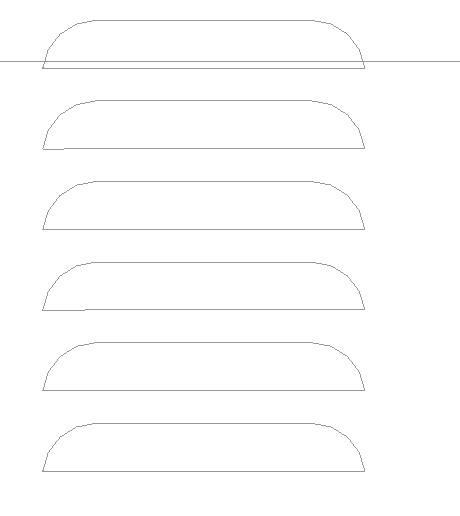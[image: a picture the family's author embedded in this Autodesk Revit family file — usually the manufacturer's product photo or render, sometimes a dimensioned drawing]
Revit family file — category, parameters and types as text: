
# Revit family: BoxAir_60-90_Inverter-P_ENG-RFA-2022
name_source: partatom
category: Mechanické zařízení
units: mm (PartAtom-declared; Revit-internal decimal feet)

## family parameters
Bod výpočtu místnosti = Ne
Kóta kulaté spojky = Použít průměr
Nadpis OmniClass = Climate Control (HVAC)
Ořezat dutým tvarem při načtení = Ne
Sdílené = Ne
Typ dílu = Normální
Vždy vertikální = Ano
Zachovat orientaci poznámky = Ne
Založené na pracovní rovině = Ne
Číslo OmniClass = 23.75.00.00

## types (2) — shared parameters
Hot water – inlet = 1'' (OD)
Hot water – outlet = 1'' (OD)
MT_CI diameter = 28 mm  [stored 0.0918635 ft]
MT_CO diameter = 28 mm  [stored 0.0918635 ft]
MT_active power = 0 W
MT_angle offset = 60 mm  [stored 0.19685 ft]
MT_apparent power = 0 VA
MT_case mat = MT_RAL7016
MT_clearance back = 250 mm  [stored 0.82021 ft]
MT_clearance top = 1500 mm  [stored 4.92126 ft]
MT_frequency (Hz) = 50 Hz
MT_ground height = 173 mm  [stored 0.567585 ft]
MT_pipe mat = MT_angle-corner
MT_voltage (V) = 400 V
Popis = Air-to-water heat pump (R290)
URL = https://www.mastertherm.eu
Výrobce = Master Therm
zero-valued in all types: Cena, MT_CosPhi, Výchozí výška

## per-type parameters (varying)
- BA60IP: El. connection=1xPG21; 1xPG29; Komentáře k typům=COMPRESSOR: BLDC Inverter; 15 – 120 rps; oil (HAF68D1U) – 2.0 l; max. op. current – 24 A; EVAPORATOR: Coil (Al/Cu); heat transfer area – 84 m2; fin spacing – 2.0 mm; max. overpress. – 3.0 MPa; max. air flow – 10000 m3/h; max. power in (fan) – 0.35 kW; fan diameter – 630 mm; speed (max.) – 900 1/min; LWA – 62 dB; defrost – reversal; CONDENSER: PHE; AISI316; water flow – 0.89 kg/s; min. flow – 0.44 kg/s; temp. difference – 5 K; water volume – 10.9 l; max. water overpress. – 250 kPa; max. refr. overpress. – 3.0 MPa; pump ext. head – 6.0 m; pump motor – 310 W; REFRIGERANT CIRCUIT: R290 (2.5 kg); PHE leak protection – 35% Propylene glycol; R290 leakage sensor – yes; AUX. HEATER: 7.5 + (7.5) kW; CONTROLS: controller – pCO5; EEV – yes; water probe – yes; SHW probe – yes; outdoor probe – yes; dynamic set point – yes; refrigerant probe – 2xPT; POWER SUPPLY: 3x400 V; 50 Hz; max. current of compressor (aux. heater) – 25 (32) A; DIMENSIONS: hot water – 1" (OD); 165x130x101 cm; 275 kg; LIMITS: max. water overpress. – 0.25 MPa; max. refr. overpress. – 2.9 MPa; air min./max.: -20/+35 °C; water min./max.: 20/65 °C; MT_TYPE=60; MT_angle length_X=1180 mm  [stored 3.87139 ft]; MT_angle length_Y=890 mm  [stored 2.91995 ft]; MT_angle length_Z=1530 mm  [stored 5.01969 ft]; MT_case depth=1010 mm  [stored 3.31365 ft]; MT_case height=1650 mm  [stored 5.41339 ft]; MT_case width=1300 mm  [stored 4.26509 ft]; MT_clearance front=3000 mm  [stored 9.84252 ft]; MT_clearance left=3000 mm  [stored 9.84252 ft]; MT_clearance right=3000 mm  [stored 9.84252 ft]; MT_cover front_X=1220 mm  [stored 4.00262 ft]; MT_cover front_Y=1570 mm; MT_cover front_Y-v2=-1010 mm  [stored -3.31365 ft]; MT_cover side_X=930 mm  [stored 3.05118 ft]; MT_cover side_Y=1570 mm; MT_cover top_X=1220 mm  [stored 4.00262 ft]; MT_cover top_Y=930 mm  [stored 3.05118 ft]; MT_front grille BA60IP W=722 mm  [stored 2.36877 ft]; MT_front grille BA90IP W=361 mm  [stored 1.18438 ft]; MT_front grille H=1570 mm; MT_grille ext front Y=1520 mm; MT_max. current – compressor (A)=25 A; MT_max. currnet – aux. heater (A)=32 A; MT_parts BA60IP_YES=Ano; MT_parts BA90IP_YES=Ne; MT_side grille H=1570 mm; MT_side grille W=445 mm  [stored 1.45997 ft]; MT_weight (kg)=230; Model=BoxAir 60 Intverter P
- BA90IP: El. connection=4xPG21; 2xPG29; Komentáře k typům=COMPRESSOR: BLDC Inverter; 15 – 120 rps; oil (RFL68EP) – 2.51 l; max. op. current – 35 A; EVAPORATOR: Coil (Al/Cu); heat transfer area – 84 m2; fin spacing – 2.0 mm; max. overpress. – 3.0 MPa; max. air flow – 15000 m3/h; max. power in (fan) – 0.7 kW; fan diameter – 2x630 mm; speed (max.) – 900 1/min; LWA – 62 dB; defrost – reversal; CONDENSER: PHE; AISI316; water flow – 1.25 kg/s; min. flow – 0.63 kg/s; temp. difference – 5 K; water volume – 10.9 l; max. water overpress. – 250 kPa; max. refr. overpress. – 3 MPa; pump ext. head – 4.0 m; pump motor – 310 W; REFRIGERANT CIRCUIT: R290 (3.5 kg); PHE leak protection – 35% Propylene glycol; R290 leakage sensor – yes; AUX. HEATER: 15 + (15) kW; CONTROLS: controller – pCO5; EEV – yes; water probe – yes; SHW probe – yes; outdoor probe – yes; dynamic set point – yes; refrigerant probe – 2xPT; POWER SUPPLY: 3x400 V; 50 Hz; max. current of compressor (aux. heater) – 40 (60) A; DIMENSIONS: hot water – 1" (OD); 168x206x104 cm; 275 kg; LIMITS: max. water overpress. – 0.25 MPa; max. refr. overpress. – 3.1 MPa; air min./max.: -20/+35 °C; water min./max.: 20/65 °C; MT_TYPE=90; MT_angle length_X=1940 mm  [stored 6.36483 ft]; MT_angle length_Y=920 mm  [stored 3.01837 ft]; MT_angle length_Z=1560 mm  [stored 5.11811 ft]; MT_case depth=1040 mm  [stored 3.41207 ft]; MT_case height=1680 mm  [stored 5.51181 ft]; MT_case width=2060 mm  [stored 6.75853 ft]; MT_clearance front=4000 mm  [stored 13.1234 ft]; MT_clearance left=4000 mm  [stored 13.1234 ft]; MT_clearance right=4000 mm  [stored 13.1234 ft]; MT_cover front_X=1980 mm  [stored 6.49606 ft]; MT_cover front_Y=1600 mm  [stored 5.24934 ft]; MT_cover front_Y-v2=-1040 mm  [stored -3.41207 ft]; MT_cover side_X=960 mm  [stored 3.14961 ft]; MT_cover side_Y=1600 mm  [stored 5.24934 ft]; MT_cover top_X=1980 mm  [stored 6.49606 ft]; MT_cover top_Y=960 mm  [stored 3.14961 ft]; MT_front grille BA60IP W=1482 mm; MT_front grille BA90IP W=741 mm  [stored 2.4311 ft]; MT_front grille H=1600 mm  [stored 5.24934 ft]; MT_grille ext front Y=1550 mm  [stored 5.0853 ft]; MT_max. current – compressor (A)=40 A; MT_max. currnet – aux. heater (A)=60 A; MT_parts BA60IP_YES=Ne; MT_parts BA90IP_YES=Ano; MT_side grille H=1600 mm  [stored 5.24934 ft]; MT_side grille W=460 mm  [stored 1.50919 ft]; MT_weight (kg)=270; Model=BoxAir 90 Intverter P

note: [stored X ft] marks values corroborated as IEEE doubles in the binary element streams (Revit-internal decimal feet)
